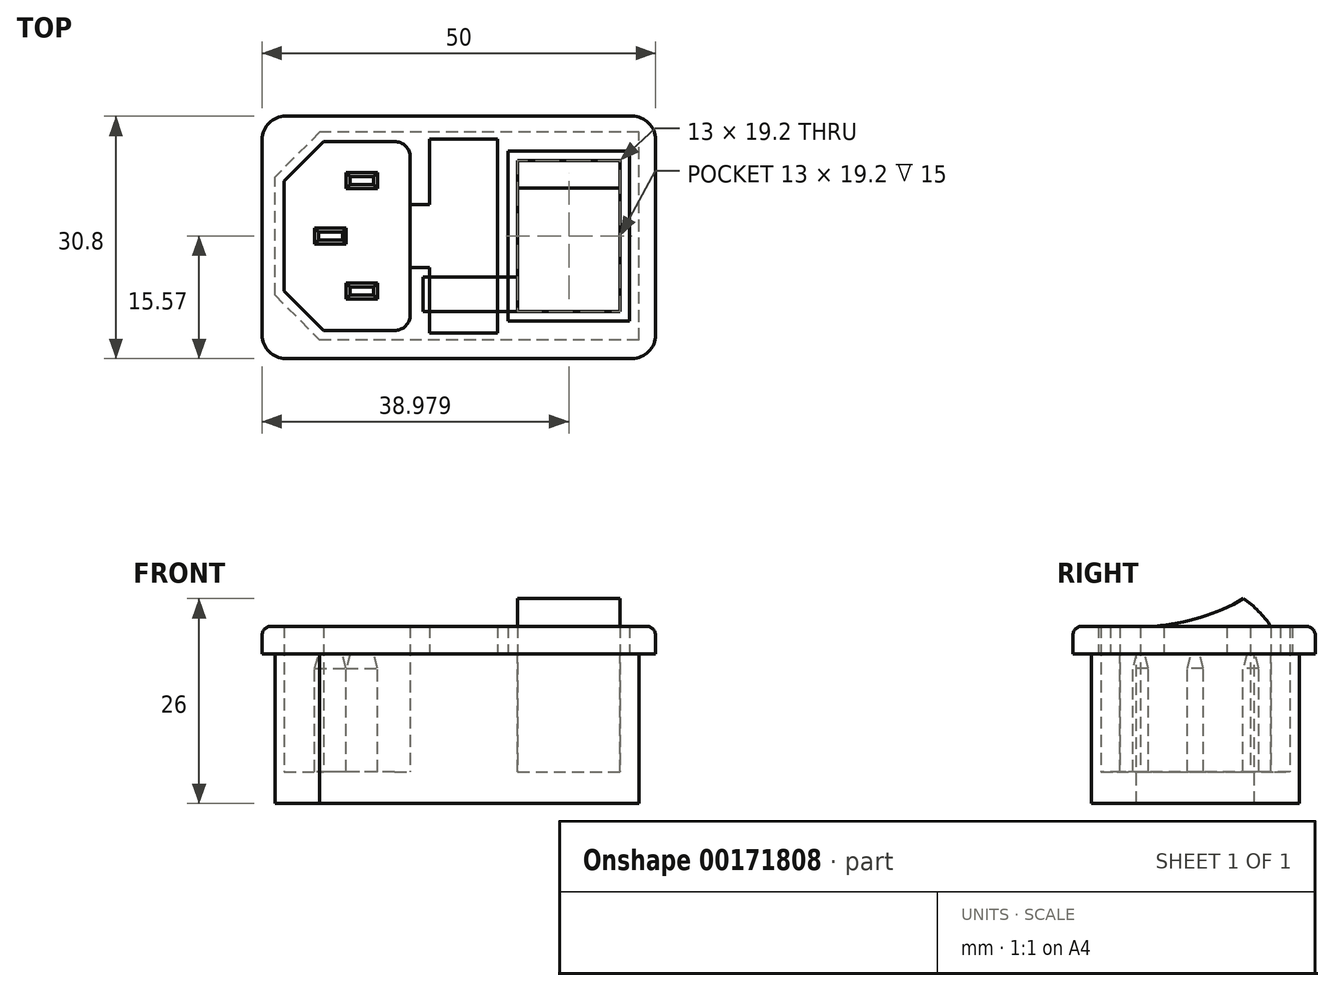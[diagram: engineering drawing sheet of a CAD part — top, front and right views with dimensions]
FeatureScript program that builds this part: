
annotation { "Feature Type Name" : "Feature", "Feature Type Description" : "" }
export const myFeature = defineFeature(function(context is Context, id is Id, definition is map)
    precondition{}
    {
        {
            var Q0;
            Q0=qCreatedBy(makeId("Top.planeOp"),FACE);
            var sketch = newSketch(context, id + "F0", { "sketchPlane" : qUnion([Q0])});
            skLineSegment(sketch, "E0.bottom", {"start": v(-22.59, 15.23) * mm, "end": v(21.41, 15.23) * mm});
            skLineSegment(sketch, "E0.top", {"start": v(-22.59, -15.57) * mm, "end": v(21.41, -15.57) * mm});
            skLineSegment(sketch, "E0.left", {"start": v(-25.59, 12.23) * mm, "end": v(-25.59, -12.57) * mm});
            skLineSegment(sketch, "E0.right", {"start": v(24.41, 12.23) * mm, "end": v(24.41, -12.57) * mm});
            skLineSegment(sketch, "E1.bottom", {"start": v(6.89, 9.6) * mm, "end": v(19.89, 9.6) * mm});
            skLineSegment(sketch, "E1.top", {"start": v(6.89, -9.6) * mm, "end": v(19.89, -9.6) * mm});
            skLineSegment(sketch, "E1.left", {"start": v(6.89, 9.6) * mm, "end": v(6.89, -9.6) * mm});
            skLineSegment(sketch, "E1.right", {"start": v(19.89, 9.6) * mm, "end": v(19.89, -9.6) * mm});
            skLineSegment(sketch, "E2.0", {"start": v(5.69, 10.8) * mm, "end": v(21.09, 10.8) * mm});
            skLineSegment(sketch, "E2.1", {"start": v(5.69, 10.8) * mm, "end": v(5.69, -10.8) * mm});
            skLineSegment(sketch, "E2.2", {"start": v(5.69, -10.8) * mm, "end": v(21.09, -10.8) * mm});
            skLineSegment(sketch, "E2.3", {"start": v(21.09, 10.8) * mm, "end": v(21.09, -10.8) * mm});
            skPoint(sketch, "E3", {"position": v(21.09, 0) * mm});
            skPoint(sketch, "E4", {"position": v(6.89, 0) * mm});
            skPoint(sketch, "E5", {"position": v(-0.59, -15.57) * mm});
            skPoint(sketch, "E6", {"position": v(-25.59, 0) * mm});
            skLineSegment(sketch, "E7.rect.bottom", {"start": v(-4.34, 12.33) * mm, "end": v(4.34, 12.33) * mm});
            skLineSegment(sketch, "E7.rect.top", {"start": v(-4.34, -12.33) * mm, "end": v(4.34, -12.33) * mm});
            skLineSegment(sketch, "E7.rect.left", {"start": v(-4.34, 12.33) * mm, "end": v(-4.34, -12.33) * mm});
            skLineSegment(sketch, "E7.rect.right", {"start": v(4.34, 12.33) * mm, "end": v(4.34, -12.33) * mm});
            skPoint(sketch, "E7.rect.middle", {"position": v(0, 0) * mm});
            skLineSegment(sketch, "E8.bottom", {"start": v(-8.76, -12) * mm, "end": v(-17.76, -12) * mm});
            skLineSegment(sketch, "E8.top", {"start": v(-8.76, 12) * mm, "end": v(-17.76, 12) * mm});
            skLineSegment(sketch, "E8.left", {"start": v(-6.76, -10) * mm, "end": v(-6.76, 10) * mm});
            skLineSegment(sketch, "E8.right", {"start": v(-22.76, -7) * mm, "end": v(-22.76, 7) * mm});
            skLineSegment(sketch, "E9", {"start": v(-17.76, 12) * mm, "end": v(-22.76, 7) * mm});
            skLineSegment(sketch, "E10", {"start": v(-22.76, -7) * mm, "end": v(-17.76, -12) * mm});
            skPoint(sketch, "E11", {"position": v(-6.76, 0) * mm});
            skPoint(sketch, "E12.visualSharp", {"position": v(24.41, 15.23) * mm});
            skArc(sketch, "E12.filletArc", {"start": v(24.41, 12.23) * mm, "mid": v(23.53, 14.35) * mm, "end": v(21.41, 15.23) * mm});
            skPoint(sketch, "E13.visualSharp", {"position": v(-25.59, 15.23) * mm});
            skArc(sketch, "E13.filletArc", {"start": v(-22.59, 15.23) * mm, "mid": v(-24.71, 14.35) * mm, "end": v(-25.59, 12.23) * mm});
            skPoint(sketch, "E14.visualSharp", {"position": v(-25.59, -15.57) * mm});
            skArc(sketch, "E14.filletArc", {"start": v(-25.59, -12.57) * mm, "mid": v(-24.71, -14.69) * mm, "end": v(-22.59, -15.57) * mm});
            skPoint(sketch, "E15.visualSharp", {"position": v(24.41, -15.57) * mm});
            skArc(sketch, "E15.filletArc", {"start": v(21.41, -15.57) * mm, "mid": v(23.53, -14.69) * mm, "end": v(24.41, -12.57) * mm});
            skPoint(sketch, "E16.visualSharp", {"position": v(-6.76, 12) * mm});
            skArc(sketch, "E16.filletArc", {"start": v(-6.76, 10) * mm, "mid": v(-7.34, 11.41) * mm, "end": v(-8.76, 12) * mm});
            skPoint(sketch, "E17.visualSharp", {"position": v(-6.76, -12) * mm});
            skArc(sketch, "E17.filletArc", {"start": v(-8.76, -12) * mm, "mid": v(-7.34, -11.41) * mm, "end": v(-6.76, -10) * mm});
            skLineSegment(sketch, "E18.rect.bottom", {"start": v(-14.89, 1) * mm, "end": v(-18.89, 1) * mm});
            skLineSegment(sketch, "E18.rect.top", {"start": v(-14.89, -1) * mm, "end": v(-18.89, -1) * mm});
            skLineSegment(sketch, "E18.rect.left", {"start": v(-14.89, 1) * mm, "end": v(-14.89, -1) * mm});
            skLineSegment(sketch, "E18.rect.right", {"start": v(-18.89, 1) * mm, "end": v(-18.89, -1) * mm});
            skPoint(sketch, "E18.rect.middle", {"position": v(-16.89, 0) * mm});
            skPoint(sketch, "E18.rect.middle.positionSnap0", {"position": v(-4.34, 0) * mm});
            skPoint(sketch, "E18.rect.centerSnap0", {"position": v(-4.34, 0) * mm});
            skLineSegment(sketch, "E19.rect.bottom", {"start": v(-10.89, 8.05) * mm, "end": v(-14.89, 8.05) * mm});
            skLineSegment(sketch, "E19.rect.right", {"start": v(-14.89, 8.05) * mm, "end": v(-14.89, 6.05) * mm});
            skLineSegment(sketch, "E19.rect.top", {"start": v(-10.89, 6.05) * mm, "end": v(-14.89, 6.05) * mm});
            skLineSegment(sketch, "E19.rect.left", {"start": v(-10.89, 8.05) * mm, "end": v(-10.89, 6.05) * mm});
            skPoint(sketch, "E19.rect.middle", {"position": v(-12.89, 7.05) * mm});
            skLineSegment(sketch, "E20.rect.bottom", {"start": v(-10.89, -5.97) * mm, "end": v(-14.89, -5.97) * mm});
            skLineSegment(sketch, "E20.rect.right", {"start": v(-14.89, -5.97) * mm, "end": v(-14.89, -7.97) * mm});
            skLineSegment(sketch, "E20.rect.top", {"start": v(-10.89, -7.97) * mm, "end": v(-14.89, -7.97) * mm});
            skLineSegment(sketch, "E20.rect.left", {"start": v(-10.89, -5.97) * mm, "end": v(-10.89, -7.97) * mm});
            skPoint(sketch, "E20.rect.middle", {"position": v(-12.89, -6.97) * mm});
            skLineSegment(sketch, "E21", {"start": v(-19.34, -78.26) * mm, "end": v(-26.2, -78.26) * mm});
            skLineSegment(sketch, "E22", {"start": v(-20.2, -74.76) * mm, "end": v(-25.73, -74.76) * mm});
            skLineSegment(sketch, "E23", {"start": v(-19.89, -48.56) * mm, "end": v(-26.2, -48.56) * mm});
            skLineSegment(sketch, "E24.0", {"start": v(-8.76, 13.2) * mm, "end": v(-18.25, 13.2) * mm});
            skLineSegment(sketch, "E24.1", {"start": v(-8.76, -13.2) * mm, "end": v(-18.25, -13.2) * mm});
            skLineSegment(sketch, "E24.2", {"start": v(-23.96, -7.5) * mm, "end": v(-18.25, -13.2) * mm});
            skLineSegment(sketch, "E24.3", {"start": v(-23.96, -7.5) * mm, "end": v(-23.96, 7.5) * mm});
            skLineSegment(sketch, "E24.4", {"start": v(-18.25, 13.2) * mm, "end": v(-23.96, 7.5) * mm});
            skLineSegment(sketch, "E25", {"start": v(-8.76, -13.2) * mm, "end": v(22.29, -13.2) * mm});
            skLineSegment(sketch, "E26", {"start": v(22.29, -13.2) * mm, "end": v(22.29, 13.2) * mm});
            skLineSegment(sketch, "E27", {"start": v(22.29, 13.2) * mm, "end": v(-8.76, 13.2) * mm});
            skLineSegment(sketch, "E28", {"start": v(-6.76, 4) * mm, "end": v(-4.34, 4) * mm});
            skLineSegment(sketch, "E29", {"start": v(-6.76, -4) * mm, "end": v(-4.34, -4) * mm});
            skSolve(sketch);
        }
        {
            var Q0;
            Q0=makeQuery(id+"F0.imprint","IMPRINT",FACE,{"disambiguationData":[TD([[makeQuery(id+"F0.imprint","IMPRINT",EDGE,{"derivedFrom":sQuery(id+"F0.wireOp",EDGE,"E0.bottom")}),-1.0]])]});
            var Q1;
            Q1=makeQuery(id+"F0.imprint","IMPRINT",FACE,{"disambiguationData":[TD([[makeQuery(id+"F0.imprint","IMPRINT",EDGE,{"derivedFrom":sQuery(id+"F0.wireOp",EDGE,"E2.0")}),1.0]])]});
            extrude(context, id + "F1", {"entities" : qUnion([Q0, Q1]), "depth" : 3.5 * mm});
        }
        {
            var Q0;
            Q0=makeQuery(id+"F0.imprint","IMPRINT",FACE,{"disambiguationData":[TD([[makeQuery(id+"F0.imprint","IMPRINT",EDGE,{"derivedFrom":sQuery(id+"F0.wireOp",EDGE,"E2.0")}),1.0]])]});
            var Q1;
            Q1=makeQuery(id+"F0.imprint","IMPRINT",FACE,{"disambiguationData":[TD([[makeQuery(id+"F0.imprint","IMPRINT",EDGE,{"derivedFrom":sQuery(id+"F0.wireOp",EDGE,"E8.bottom")}),-1.0]])]});
            var Q2;
            Q2=makeQuery(id+"F0.imprint","IMPRINT",FACE,{"disambiguationData":[TD([[makeQuery(id+"F0.imprint","IMPRINT",EDGE,{"derivedFrom":sQuery(id+"F0.wireOp",EDGE,"E1.bottom")}),-1.0]])]});
            var Q3;
            Q3=makeQuery(id+"F0.imprint","IMPRINT",FACE,{"disambiguationData":[TD([[makeQuery(id+"F0.imprint","IMPRINT",EDGE,{"derivedFrom":sQuery(id+"F0.wireOp",EDGE,"E1.bottom")}),1.0]])]});
            var Q4;
            Q4=makeQuery(id+"F0.imprint","IMPRINT",FACE,{"disambiguationData":[TD([[makeQuery(id+"F0.imprint","IMPRINT",EDGE,{"derivedFrom":sQuery(id+"F0.wireOp",EDGE,"E7.rect.bottom")}),-1.0]])]});
            var Q5;
            Q5=makeQuery(id+"F0.imprint","IMPRINT",FACE,{"disambiguationData":[TD([[makeQuery(id+"F0.imprint","IMPRINT",EDGE,{"derivedFrom":sQuery(id+"F0.wireOp",EDGE,"E20.rect.bottom")}),1.0]])]});
            var Q6;
            Q6=makeQuery(id+"F0.imprint","IMPRINT",FACE,{"disambiguationData":[TD([[makeQuery(id+"F0.imprint","IMPRINT",EDGE,{"derivedFrom":sQuery(id+"F0.wireOp",EDGE,"E18.rect.bottom")}),1.0]])]});
            var Q7;
            Q7=makeQuery(id+"F0.imprint","IMPRINT",FACE,{"disambiguationData":[TD([[makeQuery(id+"F0.imprint","IMPRINT",EDGE,{"derivedFrom":sQuery(id+"F0.wireOp",EDGE,"E19.rect.bottom")}),1.0]])]});
            var Q8;
            {var subQ0=sQuery(id+"F0.wireOp",EDGE,"E28");Q8=makeQuery(id+"F0.imprint","IMPRINT",FACE,{"disambiguationData":[TD([[makeQuery(id+"F0.imprint","IMPRINT",EDGE,{"derivedFrom":subQ0}),-1.0]])]});}
            extrude(context, id + "F2", {"entities" : qUnion([Q0, Q1, Q2, Q3, Q4, Q5, Q6, Q7, Q8]), "operationType" : NewBodyOperationType.ADD, "oppositeDirection" : true, "depth" : 19 * mm});
        }
        {
            var Q0;
            Q0=makeQuery(id+"F0.imprint","IMPRINT",FACE,{"disambiguationData":[TD([[makeQuery(id+"F0.imprint","IMPRINT",EDGE,{"derivedFrom":sQuery(id+"F0.wireOp",EDGE,"E8.bottom")}),-1.0]])]});
            var Q1;
            Q1=makeQuery(id+"F0.imprint","IMPRINT",FACE,{"disambiguationData":[TD([[makeQuery(id+"F0.imprint","IMPRINT",EDGE,{"derivedFrom":sQuery(id+"F0.wireOp",EDGE,"E1.bottom")}),-1.0]])]});
            extrude(context, id + "F3", {"entities" : qUnion([Q0, Q1]), "operationType" : NewBodyOperationType.REMOVE, "oppositeDirection" : true, "depth" : 15 * mm});
        }
        {
            var Q0;
            Q0=makeQuery(id+"F3.boolean.opBoolean","SPLIT",FACE,{"disambiguationData":[TD([makeQuery(id+"F3.opExtrude","SWEPT_FACE",FACE,{"disambiguationData":[OSD([sQuery(id+"F0.wireOp",EDGE,"E19.rect.bottom")])]})])],"derivedFrom":makeQuery(id+"F2.boolean.opBoolean","SPLIT",FACE,{"disambiguationData":[TD([makeQuery(id+"F1.opExtrude","SWEPT_FACE",FACE,{"disambiguationData":[OSD([sQuery(id+"F0.wireOp",EDGE,"E8.bottom")])]})])],"derivedFrom":makeQuery(id+"F2.opExtrude","CAP_FACE",FACE,{"disambiguationData":[OSD([sQuery(id+"F0.wireOp",EDGE,"E24.0"),sQuery(id+"F0.wireOp",EDGE,"E24.1"),sQuery(id+"F0.wireOp",EDGE,"E24.2"),sQuery(id+"F0.wireOp",EDGE,"E24.3"),sQuery(id+"F0.wireOp",EDGE,"E24.4"),sQuery(id+"F0.wireOp",EDGE,"E25"),sQuery(id+"F0.wireOp",EDGE,"E26"),sQuery(id+"F0.wireOp",EDGE,"E27")])],"isStart":true})})});
            chamfer(context, id + "F4", {"entities" : qUnion([Q0]), "chamferType" : ChamferType.OFFSET_ANGLE, "width" : 0.5 * mm, "oppositeDirection" : false, "angle" : 75 * degree, "tangentPropagation" : true});
        }
        {
            var Q0;
            Q0=makeQuery(id+"F3.boolean.opBoolean","SPLIT",FACE,{"disambiguationData":[TD([makeQuery(id+"F3.opExtrude","SWEPT_FACE",FACE,{"disambiguationData":[OSD([sQuery(id+"F0.wireOp",EDGE,"E18.rect.bottom")])]})])],"derivedFrom":makeQuery(id+"F2.boolean.opBoolean","SPLIT",FACE,{"disambiguationData":[TD([makeQuery(id+"F1.opExtrude","SWEPT_FACE",FACE,{"disambiguationData":[OSD([sQuery(id+"F0.wireOp",EDGE,"E8.bottom")])]})])],"derivedFrom":makeQuery(id+"F2.opExtrude","CAP_FACE",FACE,{"disambiguationData":[OSD([sQuery(id+"F0.wireOp",EDGE,"E24.0"),sQuery(id+"F0.wireOp",EDGE,"E24.1"),sQuery(id+"F0.wireOp",EDGE,"E24.2"),sQuery(id+"F0.wireOp",EDGE,"E24.3"),sQuery(id+"F0.wireOp",EDGE,"E24.4"),sQuery(id+"F0.wireOp",EDGE,"E25"),sQuery(id+"F0.wireOp",EDGE,"E26"),sQuery(id+"F0.wireOp",EDGE,"E27")])],"isStart":true})})});
            chamfer(context, id + "F5", {"entities" : qUnion([Q0]), "chamferType" : ChamferType.OFFSET_ANGLE, "width" : .5 * mm, "oppositeDirection" : false, "angle" : 75 * degree, "tangentPropagation" : true});
        }
        {
            var Q0;
            Q0=makeQuery(id+"F3.boolean.opBoolean","SPLIT",FACE,{"disambiguationData":[TD([makeQuery(id+"F3.opExtrude","SWEPT_FACE",FACE,{"disambiguationData":[OSD([sQuery(id+"F0.wireOp",EDGE,"E20.rect.bottom")])]})])],"derivedFrom":makeQuery(id+"F2.boolean.opBoolean","SPLIT",FACE,{"disambiguationData":[TD([makeQuery(id+"F1.opExtrude","SWEPT_FACE",FACE,{"disambiguationData":[OSD([sQuery(id+"F0.wireOp",EDGE,"E8.bottom")])]})])],"derivedFrom":makeQuery(id+"F2.opExtrude","CAP_FACE",FACE,{"disambiguationData":[OSD([sQuery(id+"F0.wireOp",EDGE,"E24.0"),sQuery(id+"F0.wireOp",EDGE,"E24.1"),sQuery(id+"F0.wireOp",EDGE,"E24.2"),sQuery(id+"F0.wireOp",EDGE,"E24.3"),sQuery(id+"F0.wireOp",EDGE,"E24.4"),sQuery(id+"F0.wireOp",EDGE,"E25"),sQuery(id+"F0.wireOp",EDGE,"E26"),sQuery(id+"F0.wireOp",EDGE,"E27")])],"isStart":true})})});
            chamfer(context, id + "F6", {"entities" : qUnion([Q0]), "chamferType" : ChamferType.OFFSET_ANGLE, "width" : .5 * mm, "oppositeDirection" : false, "angle" : 75 * degree, "tangentPropagation" : true});
        }
        {
            var Q0;
            {var subQ4=sQuery(id+"F0.wireOp",EDGE,"E7.rect.bottom");var subQ8=makeQuery(id+"F1.opExtrude","SWEPT_FACE",FACE,{"disambiguationData":[OSD([subQ4])]});Q0=makeQuery(id+"F3.boolean.opBoolean","SPLIT",FACE,{"disambiguationData":[TD([subQ8])],"derivedFrom":makeQuery(id+"F2.boolean.opBoolean","SPLIT",FACE,{"disambiguationData":[TD([subQ8])],"derivedFrom":makeQuery(id+"F2.opExtrude","CAP_FACE",FACE,{"disambiguationData":[OSD([sQuery(id+"F0.wireOp",EDGE,"E24.0"),sQuery(id+"F0.wireOp",EDGE,"E24.1"),sQuery(id+"F0.wireOp",EDGE,"E24.2"),sQuery(id+"F0.wireOp",EDGE,"E24.3"),sQuery(id+"F0.wireOp",EDGE,"E24.4"),sQuery(id+"F0.wireOp",EDGE,"E25"),sQuery(id+"F0.wireOp",EDGE,"E26"),sQuery(id+"F0.wireOp",EDGE,"E27")])],"isStart":true})})});}
            var Q1;
            Q1=makeQuery(id+"F2.boolean.opBoolean","SPLIT",FACE,{"disambiguationData":[TD([makeQuery(id+"F1.opExtrude","SWEPT_FACE",FACE,{"disambiguationData":[OSD([sQuery(id+"F0.wireOp",EDGE,"E2.0")])]})])],"derivedFrom":makeQuery(id+"F2.opExtrude","CAP_FACE",FACE,{"disambiguationData":[OSD([sQuery(id+"F0.wireOp",EDGE,"E24.0"),sQuery(id+"F0.wireOp",EDGE,"E24.1"),sQuery(id+"F0.wireOp",EDGE,"E24.2"),sQuery(id+"F0.wireOp",EDGE,"E24.3"),sQuery(id+"F0.wireOp",EDGE,"E24.4"),sQuery(id+"F0.wireOp",EDGE,"E25"),sQuery(id+"F0.wireOp",EDGE,"E26"),sQuery(id+"F0.wireOp",EDGE,"E27")])],"isStart":true})});
            var Q2;
            Q2=makeQuery(id+"F1.opExtrude","CAP_FACE",FACE,{"disambiguationData":[OSD([sQuery(id+"F0.wireOp",EDGE,"E0.bottom"),sQuery(id+"F0.wireOp",EDGE,"E0.top"),sQuery(id+"F0.wireOp",EDGE,"E0.left"),sQuery(id+"F0.wireOp",EDGE,"E0.right"),sQuery(id+"F0.wireOp",EDGE,"E2.0"),sQuery(id+"F0.wireOp",EDGE,"E2.1"),sQuery(id+"F0.wireOp",EDGE,"E2.2"),sQuery(id+"F0.wireOp",EDGE,"E2.3"),sQuery(id+"F0.wireOp",EDGE,"E7.rect.bottom"),sQuery(id+"F0.wireOp",EDGE,"E7.rect.top"),sQuery(id+"F0.wireOp",EDGE,"E7.rect.left"),sQuery(id+"F0.wireOp",EDGE,"E7.rect.right"),sQuery(id+"F0.wireOp",EDGE,"E8.bottom"),sQuery(id+"F0.wireOp",EDGE,"E8.top"),sQuery(id+"F0.wireOp",EDGE,"E8.left"),sQuery(id+"F0.wireOp",EDGE,"E8.right"),sQuery(id+"F0.wireOp",EDGE,"E9"),sQuery(id+"F0.wireOp",EDGE,"E10"),sQuery(id+"F0.wireOp",EDGE,"E12.filletArc"),sQuery(id+"F0.wireOp",EDGE,"E13.filletArc"),sQuery(id+"F0.wireOp",EDGE,"E14.filletArc"),sQuery(id+"F0.wireOp",EDGE,"E15.filletArc"),sQuery(id+"F0.wireOp",EDGE,"E16.filletArc"),sQuery(id+"F0.wireOp",EDGE,"E17.filletArc"),sQuery(id+"F0.wireOp",EDGE,"E28"),sQuery(id+"F0.wireOp",EDGE,"E29")])],"isStart":false});
            extrude(context, id + "F7", {"entities" : qUnion([Q0, Q1]), "endBound" : BoundingType.UP_TO_SURFACE, "endBoundEntityFace" : qUnion([Q2]), "depth" : 25 * mm});
        }
        {
            var Q0;
            Q0=makeQuery(id+"F3.boolean.opBoolean","COPY",FACE,{"derivedFrom":makeQuery(id+"F3.opExtrude","CAP_FACE",FACE,{"disambiguationData":[OSD([sQuery(id+"F0.wireOp",EDGE,"E1.bottom"),sQuery(id+"F0.wireOp",EDGE,"E1.top"),sQuery(id+"F0.wireOp",EDGE,"E1.left"),sQuery(id+"F0.wireOp",EDGE,"E1.right")])],"isStart":false})});
            extrude(context, id + "F8", {"entities" : qUnion([Q0]), "depth" : 22 * mm});
        }
        {
            var Q0;
            Q0=makeQuery(id+"F8.opExtrude","SWEPT_FACE",FACE,{"disambiguationData":[OSD([sQuery(id+"F0.wireOp",EDGE,"E1.right")])]});
            var sketch = newSketch(context, id + "F9", { "sketchPlane" : qUnion([Q0])});
            skLineSegment(sketch, "E30.0", {"start": v(12.23, 3.5) * mm, "end": v(-12.57, 3.5) * mm});
            skLineSegment(sketch, "E31.0", {"start": v(9.6, 7) * mm, "end": v(9.6, -15) * mm});
            skArc(sketch, "E32", {"start": v(9.6, 3.5) * mm, "mid": v(8.02, 5.4) * mm, "end": v(6.12, 7) * mm});
            skArc(sketch, "E33", {"start": v(-9.6, 3.5) * mm, "mid": v(-1.48, 4.06) * mm, "end": v(6.12, 7) * mm});
            skSolve(sketch);
        }
        {
            var Q0;
            {var subQ0=sQuery(id+"F9.wireOp",EDGE,"E33");var subQ1=sQuery(id+"F9.wireOp",EDGE,"E30.0");var subQ3=makeQuery(id+"F9.imprint","INTERSECT",VERTEX,{"derivedFrom":[subQ1,subQ0]});Q0=makeQuery(id+"F9.imprint","IMPRINT",FACE,{"disambiguationData":[TD([[makeQuery(id+"F9.imprint","IMPRINT",EDGE,{"disambiguationData":[TD([[subQ3,-1.0]])],"derivedFrom":subQ1}),1.0]])]});}
            var Q1;
            {var subQ0=sQuery(id+"F9.wireOp",EDGE,"E33");var subQ1=sQuery(id+"F9.wireOp",EDGE,"E30.0");var subQ5=makeQuery(id+"F9.imprint","INTERSECT",VERTEX,{"derivedFrom":[subQ1,subQ0]});Q1=makeQuery(id+"F9.imprint","IMPRINT",FACE,{"disambiguationData":[TD([[makeQuery(id+"F9.imprint","IMPRINT",EDGE,{"disambiguationData":[TD([[subQ5,-1.0]])],"derivedFrom":subQ0}),1.0]])]});}
            var Q2;
            {var subQ3=sQuery(id+"F9.wireOp",EDGE,"E32");Q2=makeQuery(id+"F9.imprint","IMPRINT",FACE,{"disambiguationData":[TD([[makeQuery(id+"F9.imprint","IMPRINT",EDGE,{"derivedFrom":subQ3}),-1.0]])]});}
            extrude(context, id + "F10", {"entities" : qUnion([Q0, Q1, Q2]), "operationType" : NewBodyOperationType.REMOVE, "oppositeDirection" : true, "depth" : 25 * mm});
        }
        {
            var Q0;
            Q0=makeQuery(id+"F1.opExtrude","CAP_EDGE",EDGE,{"disambiguationData":[OSD([sQuery(id+"F0.wireOp",EDGE,"E0.left")])],"isStart":false});
            fillet(context, id + "F11", {"entities" : qUnion([Q0]), "radius" : 1.2 * mm, "tangentPropagation" : true, "allowEdgeOverflow" : false});
        }
    });
